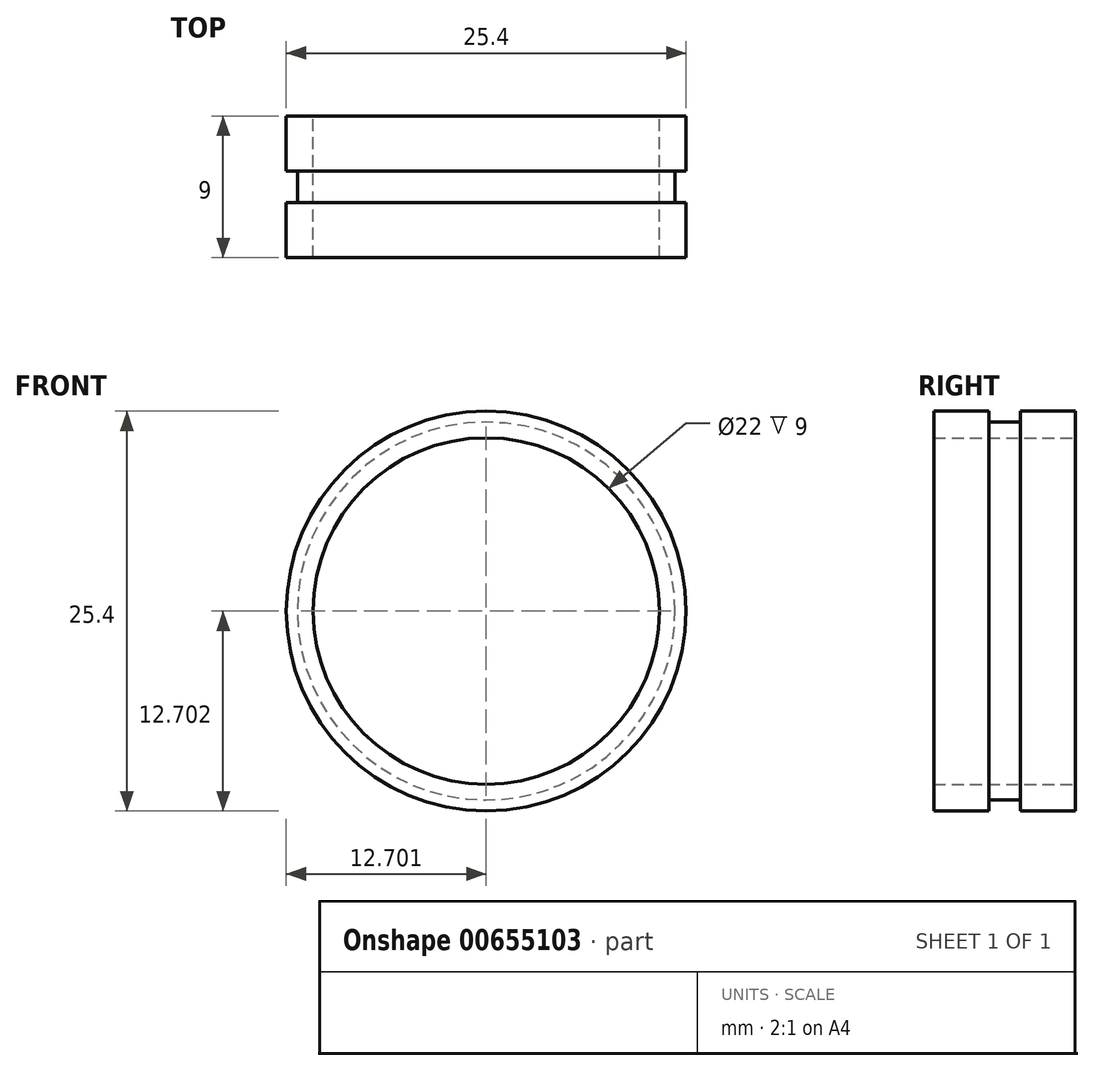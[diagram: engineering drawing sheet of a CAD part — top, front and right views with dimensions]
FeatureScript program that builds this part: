
annotation { "Feature Type Name" : "Feature", "Feature Type Description" : "" }
export const myFeature = defineFeature(function(context is Context, id is Id, definition is map)
    precondition{}
    {
        {
            var Q0;
            Q0=qCreatedBy(makeId("Front.planeOp"),FACE);
            var sketch = newSketch(context, id + "F0", { "sketchPlane" : qUnion([Q0])});
            skCircle(sketch, "E0", {"center": v(-29.93, 19.7) * mm, "radius": 12 * mm});
            skSolve(sketch);
        }
        {
            var Q0;
            Q0=makeQuery(id+"F0.imprint","IMPRINT",FACE,{"disambiguationData":[TD([[makeQuery(id+"F0.imprint","IMPRINT",EDGE,{"derivedFrom":sQuery(id+"F0.wireOp",EDGE,"4Y7z03et-453K-XJH2-AjK0-l9DA7mHbXGi9")}),1.0]])]});
            var Q1;
            Q1=makeQuery(id+"F0.imprint","IMPRINT",FACE,{"disambiguationData":[TD([[makeQuery(id+"F0.imprint","IMPRINT",EDGE,{"derivedFrom":sQuery(id+"F0.wireOp",EDGE,"E0")}),1.0]])]});
            extrude(context, id + "F1", {"entities" : qUnion([Q0, Q1]), "depth" : 9 * mm, "offsetDistance" : 25.4 * mm});
        }
        {
            var Q0;
            Q0=qCreatedBy(makeId("Front.planeOp"),FACE);
            var sketch = newSketch(context, id + "F2", { "sketchPlane" : qUnion([Q0])});
            skCircle(sketch, "E1", {"center": v(-29.93, 19.7) * mm, "radius": 12.7 * mm});
            skSolve(sketch);
        }
        {
            var Q0;
            Q0=makeQuery(id+"F2.imprint","IMPRINT",FACE,{"disambiguationData":[TD([[makeQuery(id+"F2.imprint","IMPRINT",EDGE,{"derivedFrom":sQuery(id+"F2.wireOp",EDGE,"E1")}),1.0]])]});
            extrude(context, id + "F3", {"entities" : qUnion([Q0]), "operationType" : NewBodyOperationType.ADD, "depth" : 3.5 * mm, "offsetDistance" : 25.4 * mm});
        }
        {
            var Q0;
            Q0=makeQuery(id+"F1.opExtrude","CAP_FACE",FACE,{"disambiguationData":[OSD([sQuery(id+"F0.wireOp",EDGE,"E0")])],"isStart":false});
            var sketch = newSketch(context, id + "F4", { "sketchPlane" : qUnion([Q0])});
            skCircle(sketch, "E2", {"center": v(-29.93, 19.7) * mm, "radius": 12.7 * mm});
            skSolve(sketch);
        }
        {
            var Q0;
            Q0=makeQuery(id+"F4.imprint","IMPRINT",FACE,{"disambiguationData":[TD([[makeQuery(id+"F4.imprint","IMPRINT",EDGE,{"derivedFrom":sQuery(id+"F4.wireOp",EDGE,"E2")}),1.0]])]});
            extrude(context, id + "F5", {"entities" : qUnion([Q0]), "operationType" : NewBodyOperationType.ADD, "depth" : -3.5 * mm, "offsetDistance" : 25.4 * mm});
        }
        {
            var Q0;
            Q0=sQuery(id+"F0.wireOp",VERTEX,"E0.center");
            var Q1;
            Q1=makeQuery(id+"F1.opExtrude","SWEPT_BODY",BODY,{"disambiguationData":[OSD([sQuery(id+"F0.wireOp",EDGE,"E0")])]});
            hole(context, id + "F6", {"style" : HoleStyle.SIMPLE, "endStyle" : HoleEndStyle.THROUGH, "oppositeDirection" : true, "holeDiameter" : 22 * mm, "majorDiameter" : 6.35 * mm, "isTappedThrough" : true, "tappedDepth" : 12.7 * mm, "tapClearance" : 3, "locations" : qUnion([Q0]), "scope" : qUnion([Q1])});
        }
    });
